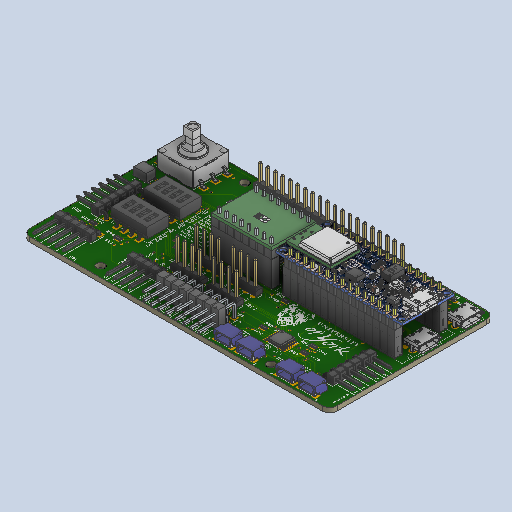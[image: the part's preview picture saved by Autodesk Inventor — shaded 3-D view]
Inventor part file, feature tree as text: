
AUTODESK INVENTOR PART (.ipt)
format: ipt  version: 2023 (Build 270158000, 158)  size: 25,899,008 bytes
history: native  units: mm
features: other x75, sketch x3
ambient origin geometry x8: Origin, YZ Plane, XZ Plane, XY Plane, X Axis, Y Axis, Z Axis, Center Point
bodies: Solid1 (feature_tree), Solid2 (feature_tree), Solid3 (feature_tree), Solid4 (feature_tree), Solid5 (feature_tree), Solid6 (feature_tree), Solid7 (feature_tree), Solid8 (feature_tree), Solid9 (feature_tree), Solid10 (feature_tree), Solid11 (feature_tree), Solid12 (feature_tree), Solid13 (feature_tree), Solid14 (feature_tree), Solid15 (feature_tree), Solid16 (feature_tree), Solid17 (feature_tree), Solid18 (feature_tree), Solid19 (feature_tree), Solid20 (feature_tree), Solid21 (feature_tree), Solid22 (feature_tree), Solid23 (feature_tree), Solid24 (feature_tree), Solid25 (feature_tree), Solid26 (feature_tree), Solid27 (feature_tree), Solid28 (feature_tree), Solid29 (feature_tree), Solid30 (feature_tree), Solid31 (feature_tree), Solid32 (feature_tree), Solid33 (feature_tree), Solid34 (feature_tree), Solid35 (feature_tree), Solid36 (feature_tree), Solid37 (feature_tree), Solid38 (feature_tree), Solid39 (feature_tree), Solid40 (feature_tree), Solid41 (feature_tree), Solid42 (feature_tree), Solid43 (feature_tree), Solid44 (feature_tree), Solid45 (feature_tree), Solid46 (feature_tree), Solid47 (feature_tree), Solid48 (feature_tree), Solid49 (feature_tree), Solid50 (feature_tree), Solid51 (feature_tree), Solid52 (feature_tree), Solid53 (feature_tree), Solid54 (feature_tree), Solid55 (feature_tree), Solid56 (feature_tree), Solid57 (feature_tree), Solid58 (feature_tree), Solid59 (feature_tree), Solid60 (feature_tree), Solid61 (feature_tree), Solid62 (feature_tree), Solid63 (feature_tree), Solid64 (feature_tree), Solid65 (feature_tree), Solid66 (feature_tree), Solid67 (feature_tree), Solid68 (feature_tree)
feature tree (78):
  other  "Main_r1.iam"
  other  "PCB Component.iam:1::Board.ipt:1"
  other  "PCB Component.iam:1::ARDUINO_NANO.iam:1::Nano33BLE.ipt:1"
  other  "PCB Component.iam:1::ARDUINO_NANO.iam:1::Female Pin Header 01x15 Pitch 2.54mm Height 8.5mm.ipt:1"
  other  "PCB Component.iam:1::ARDUINO_NANO.iam:1::Female Pin Header 01x15 Pitch 2.54mm Height 8.5mm.ipt:2"
  other  "PCB Component.iam:1::ARDUINO_NANO.iam:1::BPSC-15.ipt:1"
  other  "PCB Component.iam:1::ARDUINO_NANO.iam:1::BPSC-15.ipt:2"
  other  "PCB Component.iam:1::SOP65P640X110-16N.iam:1::Body.ipt:1"
  other  "PCB Component.iam:1::SOP65P640X110-16N.iam:1::PinsArrayLR.ipt:1"
  other  "PCB Component.iam:1::101181930001LF.ipt:1"
  other  "PCB Component.iam:1::101181930001LF.ipt:2"
  other  "PCB Component.iam:1::HDRRA6W66P0X254_1X6_1524X229X2.ipt:1"
  other  "PCB Component.iam:1::HDRRA6W66P0X254_1X6_1524X229X2.ipt:2"
  other  "PCB Component.iam:1::YC124FR0749R9L.ipt:1"
  other  "PCB Component.iam:1::YC124FR0749R9L.ipt:2"
  other  "PCB Component.iam:1::YC124FR0749R9L.ipt:3"
  other  "PCB Component.iam:1::YC124FR0749R9L.ipt:4"
  other  "PCB Component.iam:1::CAY10-XXXJ4.ipt:1"
  other  "PCB Component.iam:1::CAY10-XXXJ4.ipt:2"
  other  "PCB Component.iam:1::CAY10-XXXJ4.ipt:3"
  other  "PCB Component.iam:1::CAY10-XXXJ4.ipt:4"
  other  "PCB Component.iam:1::JS5208.ipt:1"
  other  "PCB Component.iam:1::MA05-1.ipt:1"
  other  "PCB Component.iam:1::MA05-1.ipt:2"
  other  "PCB Component.iam:1::MA05-1.ipt:3"
  other  "PCB Component.iam:1::MA05-1.ipt:4"
  other  "PCB Component.iam:1::SM04B-SRSS-TB.ipt:1"
  other  "PCB Component.iam:1::SM04B-SRSS-TB.ipt:2"
  other  "PCB Component.iam:1::SM04B-SRSS-TB.ipt:3"
  other  "PCB Component.iam:1::SM04B-SRSS-TB.ipt:4"
  other  "PCB Component.iam:1::TB6612FNG_CARRIER.iam:1::8Fx1-254mm.iam:1::Body (1).ipt:1"
  other  "PCB Component.iam:1::TB6612FNG_CARRIER.iam:1::8Fx1-254mm.iam:1::LeadsArray.ipt:1"
  other  "PCB Component.iam:1::TB6612FNG_CARRIER.iam:1::M20-9990846.iam:1::Body (1) (1).ipt:1"
  other  "PCB Component.iam:1::TB6612FNG_CARRIER.iam:1::M20-9990846.iam:1::LeadsArray (1).ipt:1"
  other  "PCB Component.iam:1::TB6612FNG_CARRIER.iam:1::tb6612fng-dual-motor-driver-carrier.ipt:1"
  other  "PCB Component.iam:1::TB6612FNG_CARRIER.iam:1::8Fx1-254mm.iam:2::Body (1).ipt:1"
  other  "PCB Component.iam:1::TB6612FNG_CARRIER.iam:1::8Fx1-254mm.iam:2::LeadsArray.ipt:1"
  other  "PCB Component.iam:1::TB6612FNG_CARRIER.iam:1::M20-9990846.iam:2::Body (1) (1).ipt:1"
  other  "PCB Component.iam:1::TB6612FNG_CARRIER.iam:1::M20-9990846.iam:2::LeadsArray (1).ipt:1"
  other  "PCB Component.iam:1::MA04-1.ipt:1"
  other  "PCB Component.iam:1::MA04-1.ipt:2"
  other  "PCB Component.iam:1::MA04-1.ipt:3"
  other  "PCB Component.iam:1::MA04-1.ipt:4"
  other  "PCB Component.iam:1::HDRRA8W64P254_2X4_1016X254X610.iam:1::Body (2).ipt:1"
  other  "PCB Component.iam:1::HDRRA8W64P254_2X4_1016X254X610.iam:1::LeadsArray (2).ipt:1"
  other  "PCB Component.iam:1::HDRRA8W64P254_2X4_1016X254X610.iam:1::LeadsArray (1) (1).ipt:1"
  other  "PCB Component.iam:1::HDRRA8W64P254_2X4_1016X254X610.iam:2::Body (2).ipt:1"
  other  "PCB Component.iam:1::HDRRA8W64P254_2X4_1016X254X610.iam:2::LeadsArray (2).ipt:1"
  other  "PCB Component.iam:1::HDRRA8W64P254_2X4_1016X254X610.iam:2::LeadsArray (1) (1).ipt:1"
  other  "PCB Component.iam:1::HDRRA4W66P0X254_1X4_1016X229X2.ipt:1"
  other  "PCB Component.iam:1::SWSO8_325X138P100.ipt:1"
  other  "PCB Component.iam:1::SWSO8_325X138P100.ipt:2"
  other  "PCB Component.iam:1::HDRRA5W66P0X254_1X5_1270X229X2.ipt:1"
  other  "PCB Component.iam:1::SO14.ipt:1"
  other  "PCB Component.iam:1::CP2102NA02GQFN20.ipt:1"
  other  "PCB Component.iam:1::C0603.ipt:1"
  other  "PCB Component.iam:1::C0603.ipt:2"
  other  "PCB Component.iam:1::R0603.ipt:1"
  other  "PCB Component.iam:1::R0603.ipt:2"
  other  "PCB Component.iam:1::R0603.ipt:3"
  other  "PCB Component.iam:1::SOT23.ipt:2"
  other  "PCB Component.iam:1::SOT23.ipt:3"
  other  "PCB Component.iam:1::SOT23.ipt:4"
  other  "PCB Component.iam:1::SOT23.ipt:5"
  other  "PCB Component.iam:1::SOT23.ipt:6"
  other  "PCB Component.iam:1::SOT23.ipt:7"
  other  "PCB Component.iam:1::SOT23.ipt:8"
  other  "PCB Component.iam:1::RKB2SJM250SMTRLFS.iam:1::Body (3).ipt:1"
  other  "PCB Component.iam:1::RKB2SJM250SMTRLFS.iam:1::Pins.ipt:1"
  sketch  "Sketch1"  dims[d0=10.0mm]
  sketch  "Sketch2"
  other  "Decal1"
  other  "Decal2"
  other  "Decal3"
  other  "Image1"
  other  "Image2"
  sketch  "Sketch3"
  other  "Image3"
